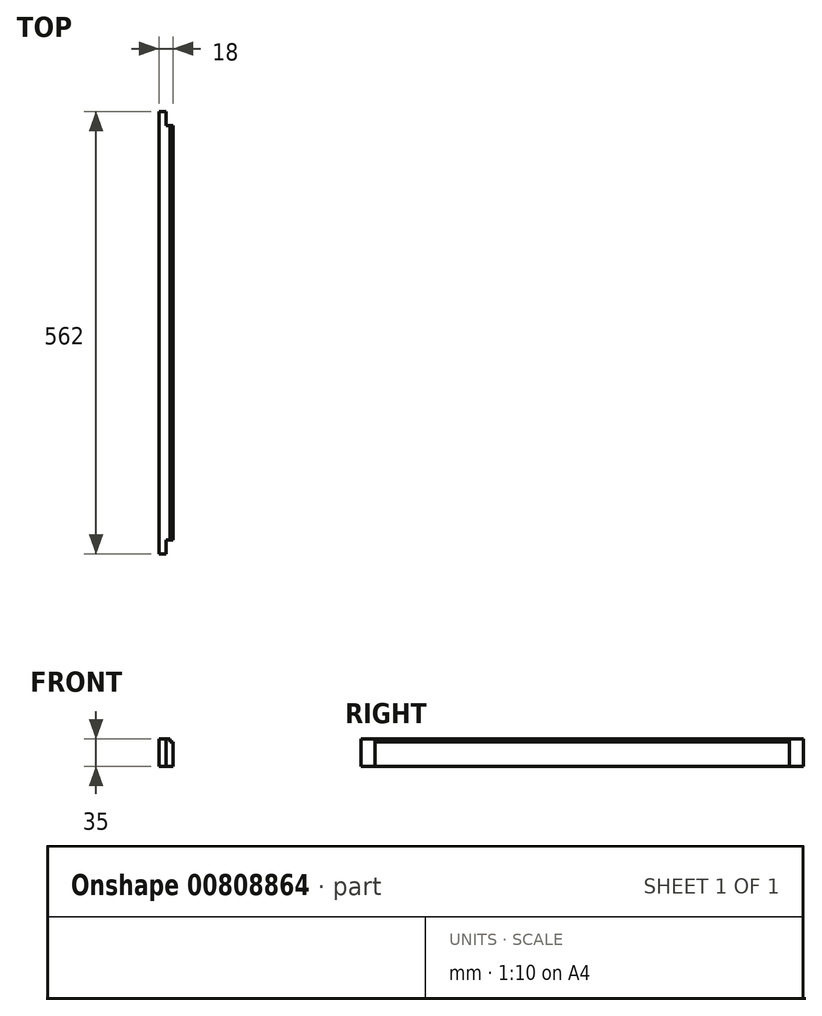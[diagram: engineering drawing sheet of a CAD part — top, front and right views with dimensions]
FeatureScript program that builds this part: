
annotation { "Feature Type Name" : "Feature", "Feature Type Description" : "" }
export const myFeature = defineFeature(function(context is Context, id is Id, definition is map)
    precondition{}
    {
        {
            var Q0;
            Q0=qCreatedBy(makeId("Right.planeOp"),FACE);
            var sketch = newSketch(context, id + "F0", { "sketchPlane" : qUnion([Q0])});
            skLineSegment(sketch, "E0.bottom", {"start": v(0, 0) * mm, "end": v(562, 0) * mm});
            skLineSegment(sketch, "E0.top", {"start": v(0, 35) * mm, "end": v(562, 35) * mm});
            skLineSegment(sketch, "E0.left", {"start": v(0, 0) * mm, "end": v(0, 35) * mm});
            skLineSegment(sketch, "E0.right", {"start": v(562, 0) * mm, "end": v(562, 35) * mm});
            skLineSegment(sketch, "E1.bottom", {"start": v(0, 35) * mm, "end": v(18, 35) * mm});
            skLineSegment(sketch, "E1.top", {"start": v(0, 0) * mm, "end": v(18, 0) * mm});
            skLineSegment(sketch, "E1.left", {"start": v(0, 35) * mm, "end": v(0, 0) * mm});
            skLineSegment(sketch, "E1.right", {"start": v(18, 35) * mm, "end": v(18, 0) * mm});
            skLineSegment(sketch, "E2.bottom", {"start": v(562, 35) * mm, "end": v(544, 35) * mm});
            skLineSegment(sketch, "E2.top", {"start": v(562, 0) * mm, "end": v(544, 0) * mm});
            skLineSegment(sketch, "E2.left", {"start": v(562, 35) * mm, "end": v(562, 0) * mm});
            skLineSegment(sketch, "E2.right", {"start": v(544, 35) * mm, "end": v(544, 0) * mm});
            skLineSegment(sketch, "E3.top", {"start": v(0, 31) * mm, "end": v(562, 31) * mm});
            skLineSegment(sketch, "E3.left", {"start": v(0, 35) * mm, "end": v(0, 31) * mm});
            skLineSegment(sketch, "E3.right", {"start": v(562, 35) * mm, "end": v(562, 31) * mm});
            skSolve(sketch);
        }
        {
            var Q0;
            {var subQ0=sQuery(id+"F0.wireOp",EDGE,"E1.right");var subQ1=sQuery(id+"F0.wireOp",EDGE,"E0.bottom");var subQ2=makeQuery(id+"F0.imprint","INTERSECT",VERTEX,{"derivedFrom":[subQ1,subQ0]});Q0=makeQuery(id+"F0.imprint","IMPRINT",FACE,{"disambiguationData":[TD([[makeQuery(id+"F0.imprint","IMPRINT",EDGE,{"disambiguationData":[TD([[subQ2,-1.0]])],"derivedFrom":subQ1}),1.0]])]});}
            extrude(context, id + "F1", {"entities" : qUnion([Q0]), "depth" : 18 * mm, "offsetDistance" : 25 * mm});
        }
        {
            var Q0;
            {var subQ0=sQuery(id+"F0.wireOp",EDGE,"E1.right");var subQ1=sQuery(id+"F0.wireOp",EDGE,"E0.bottom");var subQ2=makeQuery(id+"F0.imprint","INTERSECT",VERTEX,{"derivedFrom":[subQ1,subQ0]});Q0=makeQuery(id+"F0.imprint","IMPRINT",FACE,{"disambiguationData":[TD([[makeQuery(id+"F0.imprint","IMPRINT",EDGE,{"disambiguationData":[TD([[subQ2,1.0]])],"derivedFrom":subQ1}),1.0]])]});}
            var Q1;
            {var subQ0=sQuery(id+"F0.wireOp",EDGE,"E0.right");var subQ1=sQuery(id+"F0.wireOp",EDGE,"E0.bottom");var subQ2=makeQuery(id+"F0.imprint","INTERSECT",VERTEX,{"derivedFrom":[subQ1,subQ0]});Q1=makeQuery(id+"F0.imprint","IMPRINT",FACE,{"disambiguationData":[TD([[makeQuery(id+"F0.imprint","IMPRINT",EDGE,{"disambiguationData":[TD([[subQ2,1.0]])],"derivedFrom":subQ1}),1.0]])]});}
            var Q2;
            {var subQ0=sQuery(id+"F0.wireOp",EDGE,"E1.right");var subQ1=sQuery(id+"F0.wireOp",EDGE,"E0.top");var subQ2=makeQuery(id+"F0.imprint","INTERSECT",VERTEX,{"derivedFrom":[subQ1,subQ0]});Q2=makeQuery(id+"F0.imprint","IMPRINT",FACE,{"disambiguationData":[TD([[makeQuery(id+"F0.imprint","IMPRINT",EDGE,{"disambiguationData":[TD([[subQ2,1.0]])],"derivedFrom":subQ1}),-1.0]])]});}
            var Q3;
            {var subQ0=sQuery(id+"F0.wireOp",EDGE,"E0.right");var subQ1=sQuery(id+"F0.wireOp",EDGE,"E0.top");var subQ2=makeQuery(id+"F0.imprint","INTERSECT",VERTEX,{"derivedFrom":[subQ1,subQ0]});Q3=makeQuery(id+"F0.imprint","IMPRINT",FACE,{"disambiguationData":[TD([[makeQuery(id+"F0.imprint","IMPRINT",EDGE,{"disambiguationData":[TD([[subQ2,1.0]])],"derivedFrom":subQ1}),-1.0]])]});}
            extrude(context, id + "F2", {"entities" : qUnion([Q0, Q1, Q2, Q3]), "operationType" : NewBodyOperationType.ADD, "depth" : 9 * mm, "offsetDistance" : 25 * mm});
        }
        {
            var Q0;
            {var subQ0=sQuery(id+"F0.wireOp",EDGE,"E1.right");var subQ1=sQuery(id+"F0.wireOp",EDGE,"E0.top");var subQ2=makeQuery(id+"F0.imprint","INTERSECT",VERTEX,{"derivedFrom":[subQ1,subQ0]});Q0=makeQuery(id+"F0.imprint","IMPRINT",FACE,{"disambiguationData":[TD([[makeQuery(id+"F0.imprint","IMPRINT",EDGE,{"disambiguationData":[TD([[subQ2,-1.0]])],"derivedFrom":subQ1}),-1.0]])]});}
            extrude(context, id + "F3", {"entities" : qUnion([Q0]), "operationType" : NewBodyOperationType.ADD, "depth" : 14 * mm, "offsetDistance" : 25 * mm});
        }
    });
